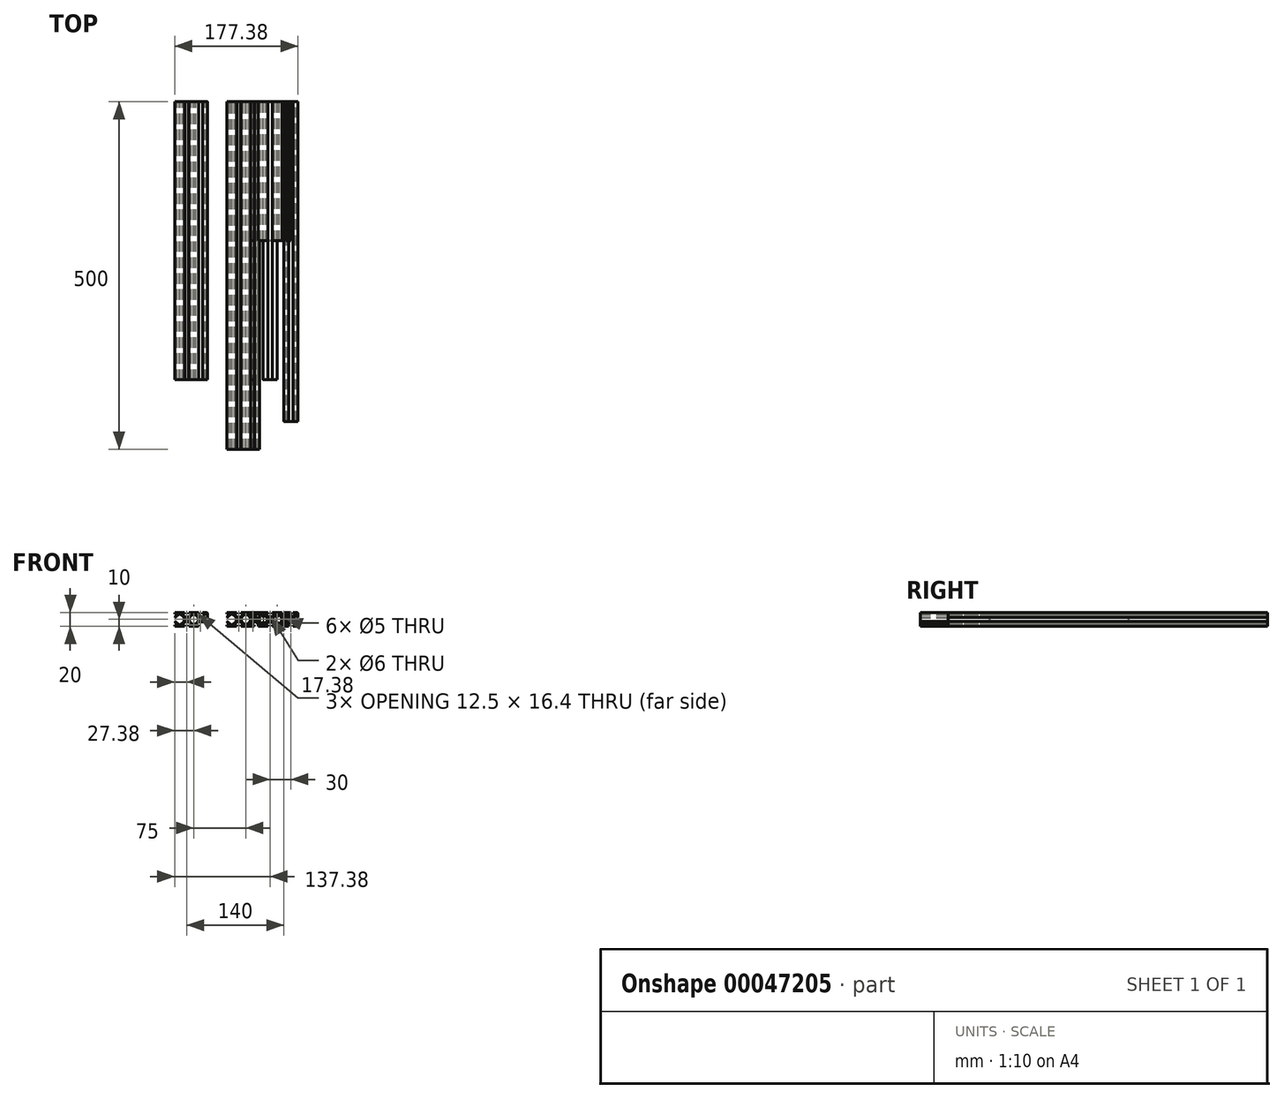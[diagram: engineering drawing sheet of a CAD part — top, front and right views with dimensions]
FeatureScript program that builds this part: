
annotation { "Feature Type Name" : "Feature", "Feature Type Description" : "" }
export const myFeature = defineFeature(function(context is Context, id is Id, definition is map)
    precondition{}
    {
        {
            var Q0;
            Q0=qCreatedBy(makeId("Front.planeOp"),FACE);
            var sketch = newSketch(context, id + "F0", { "sketchPlane" : qUnion([Q0])});
            skLineSegment(sketch, "E0.rect.bottom", {"start": v(8.5, -10) * mm, "end": v(3, -10) * mm});
            skLineSegment(sketch, "E0.rect.top", {"start": v(8.5, 10) * mm, "end": v(3, 10) * mm});
            skLineSegment(sketch, "E0.rect.left", {"start": v(10, -8.5) * mm, "end": v(10, -3) * mm});
            skLineSegment(sketch, "E0.rect.right", {"start": v(-10, -8.5) * mm, "end": v(-10, -3) * mm});
            skPoint(sketch, "E0.rect.middle", {"position": v(0, 0) * mm});
            skCircle(sketch, "E1", {"center": v(0, 0) * mm, "radius": 3 * mm});
            skPoint(sketch, "E2.visualSharp", {"position": v(-10, -10) * mm});
            skArc(sketch, "E2.filletArc", {"start": v(-10, -8.5) * mm, "mid": v(-9.56, -9.56) * mm, "end": v(-8.5, -10) * mm});
            skPoint(sketch, "E3.visualSharp", {"position": v(10, -10) * mm});
            skArc(sketch, "E3.filletArc", {"start": v(8.5, -10) * mm, "mid": v(9.56, -9.56) * mm, "end": v(10, -8.5) * mm});
            skPoint(sketch, "E4.visualSharp", {"position": v(10, 10) * mm});
            skArc(sketch, "E4.filletArc", {"start": v(10, 8.5) * mm, "mid": v(9.56, 9.56) * mm, "end": v(8.5, 10) * mm});
            skPoint(sketch, "E5.visualSharp", {"position": v(-10, 10) * mm});
            skArc(sketch, "E5.filletArc", {"start": v(-8.5, 10) * mm, "mid": v(-9.56, 9.56) * mm, "end": v(-10, 8.5) * mm});
            skLineSegment(sketch, "E6.rect.bottom", {"start": v(4.25, -4.25) * mm, "end": v(-4.25, -4.25) * mm});
            skLineSegment(sketch, "E6.rect.top", {"start": v(4.25, 4.25) * mm, "end": v(-4.25, 4.25) * mm});
            skLineSegment(sketch, "E6.rect.left", {"start": v(4.25, -4.25) * mm, "end": v(4.25, 4.25) * mm});
            skLineSegment(sketch, "E6.rect.right", {"start": v(-4.25, -4.25) * mm, "end": v(-4.25, 4.25) * mm});
            skLineSegment(sketch, "E7", {"start": v(-3, -10) * mm, "end": v(-3, -8.5) * mm});
            skLineSegment(sketch, "E8", {"start": v(-3, -8.5) * mm, "end": v(-6, -8.5) * mm});
            skLineSegment(sketch, "E9", {"start": v(-6, -8.5) * mm, "end": v(-6, -7) * mm});
            skLineSegment(sketch, "E10", {"start": v(-6, -7) * mm, "end": v(-3.25, -4.25) * mm});
            skLineSegment(sketch, "E11.MirrorCS", {"start": v(3, -10) * mm, "end": v(3, -8.5) * mm});
            skLineSegment(sketch, "E12.MirrorCS", {"start": v(3, -8.5) * mm, "end": v(6, -8.5) * mm});
            skLineSegment(sketch, "E13.MirrorCS", {"start": v(6, -8.5) * mm, "end": v(6, -7) * mm});
            skLineSegment(sketch, "E14.MirrorCS", {"start": v(6, -7) * mm, "end": v(3.25, -4.25) * mm});
            skLineSegment(sketch, "E15.MirrorCS", {"start": v(6, 7) * mm, "end": v(3.25, 4.25) * mm});
            skLineSegment(sketch, "E16.MirrorCS", {"start": v(6, 8.5) * mm, "end": v(6, 7) * mm});
            skLineSegment(sketch, "E17.MirrorCS", {"start": v(3, 8.5) * mm, "end": v(6, 8.5) * mm});
            skLineSegment(sketch, "E18.MirrorCS", {"start": v(3, 10) * mm, "end": v(3, 8.5) * mm});
            skLineSegment(sketch, "E19.MirrorCS", {"start": v(-3, 10) * mm, "end": v(-3, 8.5) * mm});
            skLineSegment(sketch, "E20.MirrorCS", {"start": v(-3, 8.5) * mm, "end": v(-6, 8.5) * mm});
            skLineSegment(sketch, "E21.MirrorCS", {"start": v(-6, 8.5) * mm, "end": v(-6, 7) * mm});
            skLineSegment(sketch, "E22.MirrorCS", {"start": v(-6, 7) * mm, "end": v(-3.25, 4.25) * mm});
            skLineSegment(sketch, "E23", {"start": v(-10, -10) * mm, "end": v(10, 10) * mm, "construction": true});
            skLineSegment(sketch, "E24.MirrorCS", {"start": v(-8.5, 3) * mm, "end": v(-8.5, 6) * mm});
            skLineSegment(sketch, "E25.MirrorCS", {"start": v(-8.5, 6) * mm, "end": v(-7, 6) * mm});
            skLineSegment(sketch, "E26.MirrorCS", {"start": v(-10, -3) * mm, "end": v(-8.5, -3) * mm});
            skLineSegment(sketch, "E27.MirrorCS", {"start": v(-10, 3) * mm, "end": v(-8.5, 3) * mm});
            skLineSegment(sketch, "E28.MirrorCS", {"start": v(-8.5, -6) * mm, "end": v(-7, -6) * mm});
            skLineSegment(sketch, "E29.MirrorCS", {"start": v(-8.5, -3) * mm, "end": v(-8.5, -6) * mm});
            skLineSegment(sketch, "E30.MirrorCS", {"start": v(-7, 6) * mm, "end": v(-4.25, 3.25) * mm});
            skLineSegment(sketch, "E31.MirrorCS", {"start": v(-7, -6) * mm, "end": v(-4.25, -3.25) * mm});
            skLineSegment(sketch, "E32.MirrorCS", {"start": v(8.5, -6) * mm, "end": v(7, -6) * mm});
            skLineSegment(sketch, "E33.MirrorCS", {"start": v(8.5, 6) * mm, "end": v(7, 6) * mm});
            skLineSegment(sketch, "E34.MirrorCS", {"start": v(10, 3) * mm, "end": v(8.5, 3) * mm});
            skLineSegment(sketch, "E35.MirrorCS", {"start": v(7, -6) * mm, "end": v(4.25, -3.25) * mm});
            skLineSegment(sketch, "E36.MirrorCS", {"start": v(8.5, -3) * mm, "end": v(8.5, -6) * mm});
            skLineSegment(sketch, "E37.MirrorCS", {"start": v(8.5, 3) * mm, "end": v(8.5, 6) * mm});
            skLineSegment(sketch, "E38.MirrorCS", {"start": v(7, 6) * mm, "end": v(4.25, 3.25) * mm});
            skLineSegment(sketch, "E39.MirrorCS", {"start": v(10, -3) * mm, "end": v(8.5, -3) * mm});
            skLineSegment(sketch, "E40.trimOffspring", {"start": v(-3, -10) * mm, "end": v(-8.5, -10) * mm});
            skLineSegment(sketch, "E41.trimOffspring", {"start": v(10, 3) * mm, "end": v(10, 8.5) * mm});
            skLineSegment(sketch, "E42.trimOffspring", {"start": v(-3, 10) * mm, "end": v(-8.5, 10) * mm});
            skLineSegment(sketch, "E43.trimOffspring", {"start": v(-10, 3) * mm, "end": v(-10, 8.5) * mm});
            skSolve(sketch);
        }
        {
            var Q0;
            Q0=makeQuery(id+"F0.imprint","IMPRINT",FACE,{"disambiguationData":[TD([[makeQuery(id+"F0.imprint","IMPRINT",EDGE,{"derivedFrom":sQuery(id+"F0.wireOp",EDGE,"E0.rect.right")}),-1.0]])]});
            var Q1;
            Q1=makeQuery(id+"F0.imprint","IMPRINT",FACE,{"disambiguationData":[TD([[makeQuery(id+"F0.imprint","IMPRINT",EDGE,{"derivedFrom":sQuery(id+"F0.wireOp",EDGE,"E1")}),-1.0]])]});
            var Q2;
            Q2=makeQuery(id+"F0.imprint","IMPRINT",FACE,{"disambiguationData":[TD([[makeQuery(id+"F0.imprint","IMPRINT",EDGE,{"derivedFrom":sQuery(id+"F0.wireOp",EDGE,"E0.rect.bottom")}),-1.0]])]});
            var Q3;
            Q3=makeQuery(id+"F0.imprint","IMPRINT",FACE,{"disambiguationData":[TD([[makeQuery(id+"F0.imprint","IMPRINT",EDGE,{"derivedFrom":sQuery(id+"F0.wireOp",EDGE,"E0.rect.top")}),1.0]])]});
            var Q4;
            Q4=makeQuery(id+"F0.imprint","IMPRINT",FACE,{"disambiguationData":[TD([[makeQuery(id+"F0.imprint","IMPRINT",EDGE,{"derivedFrom":sQuery(id+"F0.wireOp",EDGE,"E5.filletArc")}),1.0]])]});
            extrude(context, id + "F1", {"entities" : qUnion([Q0, Q1, Q2, Q3, Q4]), "depth" : 460 * mm});
        }
        {
            var Q0;
            Q0=makeQuery(id+"F0.imprint","IMPRINT",FACE,{"disambiguationData":[TD([[makeQuery(id+"F0.imprint","IMPRINT",EDGE,{"derivedFrom":sQuery(id+"F0.wireOp",EDGE,"E0.rect.right")}),-1.0]])]});
            var Q1;
            Q1=makeQuery(id+"F0.imprint","IMPRINT",FACE,{"disambiguationData":[TD([[makeQuery(id+"F0.imprint","IMPRINT",EDGE,{"derivedFrom":sQuery(id+"F0.wireOp",EDGE,"E1")}),-1.0]])]});
            var Q2;
            Q2=makeQuery(id+"F0.imprint","IMPRINT",FACE,{"disambiguationData":[TD([[makeQuery(id+"F0.imprint","IMPRINT",EDGE,{"derivedFrom":sQuery(id+"F0.wireOp",EDGE,"E0.rect.bottom")}),-1.0]])]});
            var Q3;
            Q3=makeQuery(id+"F0.imprint","IMPRINT",FACE,{"disambiguationData":[TD([[makeQuery(id+"F0.imprint","IMPRINT",EDGE,{"derivedFrom":sQuery(id+"F0.wireOp",EDGE,"E0.rect.top")}),1.0]])]});
            var Q4;
            Q4=makeQuery(id+"F0.imprint","IMPRINT",FACE,{"disambiguationData":[TD([[makeQuery(id+"F0.imprint","IMPRINT",EDGE,{"derivedFrom":sQuery(id+"F0.wireOp",EDGE,"E5.filletArc")}),1.0]])]});
            extrude(context, id + "F2", {"entities" : qUnion([Q0, Q1, Q2, Q3, Q4]), "depth" : 400 * mm});
        }
        {
            var Q0;
            Q0=makeQuery(id+"F1.opExtrude","SWEPT_BODY",BODY,{"disambiguationData":[OSD([sQuery(id+"F0.wireOp",EDGE,"E0.rect.bottom"),sQuery(id+"F0.wireOp",EDGE,"E0.rect.top"),sQuery(id+"F0.wireOp",EDGE,"E0.rect.left"),sQuery(id+"F0.wireOp",EDGE,"E0.rect.right"),sQuery(id+"F0.wireOp",EDGE,"E1"),sQuery(id+"F0.wireOp",EDGE,"E2.filletArc"),sQuery(id+"F0.wireOp",EDGE,"E3.filletArc"),sQuery(id+"F0.wireOp",EDGE,"E4.filletArc"),sQuery(id+"F0.wireOp",EDGE,"E5.filletArc"),sQuery(id+"F0.wireOp",EDGE,"E6.rect.bottom"),sQuery(id+"F0.wireOp",EDGE,"E6.rect.top"),sQuery(id+"F0.wireOp",EDGE,"E6.rect.right"),sQuery(id+"F0.wireOp",EDGE,"E7"),sQuery(id+"F0.wireOp",EDGE,"E8"),sQuery(id+"F0.wireOp",EDGE,"E9"),sQuery(id+"F0.wireOp",EDGE,"E10"),sQuery(id+"F0.wireOp",EDGE,"E11.MirrorCS"),sQuery(id+"F0.wireOp",EDGE,"E12.MirrorCS"),sQuery(id+"F0.wireOp",EDGE,"E13.MirrorCS"),sQuery(id+"F0.wireOp",EDGE,"E14.MirrorCS"),sQuery(id+"F0.wireOp",EDGE,"E15.MirrorCS"),sQuery(id+"F0.wireOp",EDGE,"E16.MirrorCS"),sQuery(id+"F0.wireOp",EDGE,"E17.MirrorCS"),sQuery(id+"F0.wireOp",EDGE,"E18.MirrorCS"),sQuery(id+"F0.wireOp",EDGE,"E19.MirrorCS"),sQuery(id+"F0.wireOp",EDGE,"E20.MirrorCS"),sQuery(id+"F0.wireOp",EDGE,"E21.MirrorCS"),sQuery(id+"F0.wireOp",EDGE,"E22.MirrorCS"),sQuery(id+"F0.wireOp",EDGE,"E24.MirrorCS"),sQuery(id+"F0.wireOp",EDGE,"E25.MirrorCS"),sQuery(id+"F0.wireOp",EDGE,"E26.MirrorCS"),sQuery(id+"F0.wireOp",EDGE,"E27.MirrorCS"),sQuery(id+"F0.wireOp",EDGE,"E28.MirrorCS"),sQuery(id+"F0.wireOp",EDGE,"E29.MirrorCS"),sQuery(id+"F0.wireOp",EDGE,"E30.MirrorCS"),sQuery(id+"F0.wireOp",EDGE,"E31.MirrorCS"),sQuery(id+"F0.wireOp",EDGE,"E32.MirrorCS"),sQuery(id+"F0.wireOp",EDGE,"E33.MirrorCS"),sQuery(id+"F0.wireOp",EDGE,"E34.MirrorCS"),sQuery(id+"F0.wireOp",EDGE,"E35.MirrorCS"),sQuery(id+"F0.wireOp",EDGE,"E36.MirrorCS"),sQuery(id+"F0.wireOp",EDGE,"E37.MirrorCS"),sQuery(id+"F0.wireOp",EDGE,"E6.rect.left"),sQuery(id+"F0.wireOp",EDGE,"E38.MirrorCS"),sQuery(id+"F0.wireOp",EDGE,"E39.MirrorCS"),sQuery(id+"F0.wireOp",EDGE,"E40.trimOffspring"),sQuery(id+"F0.wireOp",EDGE,"E41.trimOffspring"),sQuery(id+"F0.wireOp",EDGE,"E42.trimOffspring"),sQuery(id+"F0.wireOp",EDGE,"E43.trimOffspring")])]});
            transform(context, id + "F3", {"entities" : qUnion([Q0]), "transformType" : TransformType.TRANSLATION_3D, "dx" : 30 * mm, "dy" : 0 * mm, "dz" : 0 * mm, "makeCopy" : false});
        }
        {
            var Q0;
            Q0=qCreatedBy(makeId("Front.planeOp"),FACE);
            var sketch = newSketch(context, id + "F4", { "sketchPlane" : qUnion([Q0])});
            skLineSegment(sketch, "E44.rect.bottom", {"start": v(28.5, 10) * mm, "end": v(3, 10) * mm});
            skLineSegment(sketch, "E44.rect.top", {"start": v(28.5, -10) * mm, "end": v(3, -10) * mm});
            skLineSegment(sketch, "E44.rect.left", {"start": v(30, 8.5) * mm, "end": v(30, -8.5) * mm});
            skLineSegment(sketch, "E44.rect.right", {"start": v(-30, 8.5) * mm, "end": v(-30, -8.5) * mm});
            skPoint(sketch, "E44.rect.middle", {"position": v(0, 0) * mm});
            skPoint(sketch, "E45.visualSharp", {"position": v(-30, 10) * mm});
            skArc(sketch, "E45.filletArc", {"start": v(-28.5, 10) * mm, "mid": v(-29.56, 9.56) * mm, "end": v(-30, 8.5) * mm});
            skPoint(sketch, "E46.visualSharp", {"position": v(30, 10) * mm});
            skArc(sketch, "E46.filletArc", {"start": v(30, 8.5) * mm, "mid": v(29.56, 9.56) * mm, "end": v(28.5, 10) * mm});
            skPoint(sketch, "E47.visualSharp", {"position": v(30, -10) * mm});
            skArc(sketch, "E47.filletArc", {"start": v(28.5, -10) * mm, "mid": v(29.56, -9.56) * mm, "end": v(30, -8.5) * mm});
            skPoint(sketch, "E48.visualSharp", {"position": v(-30, -10) * mm});
            skArc(sketch, "E48.filletArc", {"start": v(-30, -8.5) * mm, "mid": v(-29.56, -9.56) * mm, "end": v(-28.5, -10) * mm});
            skCircle(sketch, "E49", {"center": v(0, 0) * mm, "radius": 2.5 * mm});
            skLineSegment(sketch, "E50", {"start": v(-3, 10) * mm, "end": v(-3, 8.2) * mm});
            skLineSegment(sketch, "E51", {"start": v(-3, 8.2) * mm, "end": v(-5.86, 8.2) * mm});
            skLineSegment(sketch, "E52.rect.bottom", {"start": v(3.75, 3.75) * mm, "end": v(-3.75, 3.75) * mm});
            skLineSegment(sketch, "E52.rect.top", {"start": v(3.75, -3.75) * mm, "end": v(-3.75, -3.75) * mm});
            skLineSegment(sketch, "E52.rect.left", {"start": v(3.75, 3.75) * mm, "end": v(3.75, -3.75) * mm});
            skLineSegment(sketch, "E52.rect.right", {"start": v(-3.75, 3.75) * mm, "end": v(-3.75, -3.75) * mm});
            skLineSegment(sketch, "E53", {"start": v(-6.22, 7.35) * mm, "end": v(-2.62, 3.75) * mm});
            skLineSegment(sketch, "E54.MirrorCS", {"start": v(3, 10) * mm, "end": v(3, 8.2) * mm});
            skLineSegment(sketch, "E55.MirrorCS", {"start": v(3, 8.2) * mm, "end": v(5.86, 8.2) * mm});
            skLineSegment(sketch, "E56.MirrorCS", {"start": v(6.22, 7.35) * mm, "end": v(2.62, 3.75) * mm});
            skLineSegment(sketch, "E57", {"start": v(-3.75, 3.75) * mm, "end": v(3.75, -3.75) * mm, "construction": true});
            skLineSegment(sketch, "E58.MirrorCS", {"start": v(-8.2, 7.07) * mm, "end": v(-3.75, 2.62) * mm});
            skLineSegment(sketch, "E59.MirrorCS", {"start": v(-8.2, -7.07) * mm, "end": v(-3.75, -2.62) * mm});
            skLineSegment(sketch, "E60.MirrorCS", {"start": v(-3, -8.2) * mm, "end": v(-5.86, -8.2) * mm});
            skLineSegment(sketch, "E61.MirrorCS", {"start": v(-3, -10) * mm, "end": v(-3, -8.2) * mm});
            skLineSegment(sketch, "E62.MirrorCS", {"start": v(-6.22, -7.35) * mm, "end": v(-2.62, -3.75) * mm});
            skLineSegment(sketch, "E63.MirrorCS", {"start": v(3, -8.2) * mm, "end": v(5.86, -8.2) * mm});
            skLineSegment(sketch, "E64.MirrorCS", {"start": v(6.22, -7.35) * mm, "end": v(2.62, -3.75) * mm});
            skLineSegment(sketch, "E65.MirrorCS", {"start": v(3, -10) * mm, "end": v(3, -8.2) * mm});
            skLineSegment(sketch, "E66", {"start": v(-8.2, 7.07) * mm, "end": v(-9.33, 8.2) * mm});
            skLineSegment(sketch, "E67.trimOffspring", {"start": v(-3, 10) * mm, "end": v(-17, 10) * mm});
            skLineSegment(sketch, "E68.trimOffspring", {"start": v(-3, -10) * mm, "end": v(-17, -10) * mm});
            skPoint(sketch, "E69.visualSharp", {"position": v(-7.07, 8.2) * mm});
            skArc(sketch, "E69.filletArc", {"start": v(-5.86, 8.2) * mm, "mid": v(-6.32, 7.9) * mm, "end": v(-6.22, 7.35) * mm});
            skPoint(sketch, "E70.visualSharp", {"position": v(7.07, 8.2) * mm});
            skArc(sketch, "E70.filletArc", {"start": v(6.22, 7.35) * mm, "mid": v(6.32, 7.9) * mm, "end": v(5.86, 8.2) * mm});
            skPoint(sketch, "E71.visualSharp", {"position": v(7.07, -8.2) * mm});
            skArc(sketch, "E71.filletArc", {"start": v(5.86, -8.2) * mm, "mid": v(6.32, -7.9) * mm, "end": v(6.22, -7.35) * mm});
            skPoint(sketch, "E72.visualSharp", {"position": v(-7.07, -8.2) * mm});
            skArc(sketch, "E72.filletArc", {"start": v(-6.22, -7.35) * mm, "mid": v(-6.32, -7.9) * mm, "end": v(-5.86, -8.2) * mm});
            skLineSegment(sketch, "E73", {"start": v(-10, 13.64) * mm, "end": v(-10, -16.65) * mm, "construction": true});
            skLineSegment(sketch, "E74", {"start": v(-9.33, 8.2) * mm, "end": v(-10, 8.2) * mm});
            skLineSegment(sketch, "E75.MirrorCS", {"start": v(-8.2, -7.07) * mm, "end": v(-9.33, -8.2) * mm});
            skLineSegment(sketch, "E76.MirrorCS", {"start": v(-9.33, -8.2) * mm, "end": v(-10, -8.2) * mm});
            skLineSegment(sketch, "E77.MirrorCS", {"start": v(-17, -10) * mm, "end": v(-17, -8.2) * mm});
            skLineSegment(sketch, "E78.MirrorCS", {"start": v(-11.8, -7.07) * mm, "end": v(-16.25, -2.62) * mm});
            skPoint(sketch, "E79.MirrorP", {"position": v(-20, 0) * mm});
            skLineSegment(sketch, "E80.MirrorCS", {"start": v(-23, -10) * mm, "end": v(-23, -8.2) * mm});
            skLineSegment(sketch, "E81.MirrorCS", {"start": v(-13.78, -7.35) * mm, "end": v(-17.38, -3.75) * mm});
            skPoint(sketch, "E82.MirrorP", {"position": v(-12.93, -8.2) * mm});
            skLineSegment(sketch, "E83.MirrorCS", {"start": v(-23, 8.2) * mm, "end": v(-25.86, 8.2) * mm});
            skLineSegment(sketch, "E84.MirrorCS", {"start": v(-11.8, 7.07) * mm, "end": v(-10.67, 8.2) * mm});
            skPoint(sketch, "E85.MirrorP", {"position": v(-27.07, -8.2) * mm});
            skPoint(sketch, "E86.MirrorP", {"position": v(-12.93, 8.2) * mm});
            skLineSegment(sketch, "E87.MirrorCS", {"start": v(-26.22, -7.35) * mm, "end": v(-22.62, -3.75) * mm});
            skLineSegment(sketch, "E88.MirrorCS", {"start": v(-11.8, -7.07) * mm, "end": v(-10.67, -8.2) * mm});
            skLineSegment(sketch, "E89.MirrorCS", {"start": v(-11.8, 7.07) * mm, "end": v(-16.25, 2.62) * mm});
            skLineSegment(sketch, "E90.MirrorCS", {"start": v(-17, 10) * mm, "end": v(-17, 8.2) * mm});
            skLineSegment(sketch, "E91.MirrorCS", {"start": v(-17, 8.2) * mm, "end": v(-14.14, 8.2) * mm});
            skCircle(sketch, "E92.MirrorC", {"center": v(-20, 0) * mm, "radius": 2.5 * mm});
            skLineSegment(sketch, "E93.MirrorCS", {"start": v(-23, 10) * mm, "end": v(-23, 8.2) * mm});
            skLineSegment(sketch, "E94.MirrorCS", {"start": v(-16.25, 3.75) * mm, "end": v(-23.75, -3.75) * mm, "construction": true});
            skLineSegment(sketch, "E95.MirrorCS", {"start": v(-17, -8.2) * mm, "end": v(-14.14, -8.2) * mm});
            skArc(sketch, "E96.MirrorCS", {"start": v(-25.86, -8.2) * mm, "mid": v(-26.32, -7.9) * mm, "end": v(-26.22, -7.35) * mm});
            skArc(sketch, "E97.MirrorCS", {"start": v(-26.22, 7.35) * mm, "mid": v(-26.32, 7.9) * mm, "end": v(-25.86, 8.2) * mm});
            skArc(sketch, "E98.MirrorCS", {"start": v(-13.78, -7.35) * mm, "mid": v(-13.68, -7.9) * mm, "end": v(-14.14, -8.2) * mm});
            skPoint(sketch, "E99.MirrorP", {"position": v(-27.07, 8.2) * mm});
            skLineSegment(sketch, "E100.MirrorCS", {"start": v(-26.22, 7.35) * mm, "end": v(-22.62, 3.75) * mm});
            skArc(sketch, "E101.MirrorCS", {"start": v(-14.14, 8.2) * mm, "mid": v(-13.68, 7.9) * mm, "end": v(-13.78, 7.35) * mm});
            skLineSegment(sketch, "E102.MirrorCS", {"start": v(-23.75, -3.75) * mm, "end": v(-16.25, -3.75) * mm});
            skLineSegment(sketch, "E103.MirrorCS", {"start": v(-23.75, 3.75) * mm, "end": v(-16.25, 3.75) * mm});
            skLineSegment(sketch, "E104.MirrorCS", {"start": v(-13.78, 7.35) * mm, "end": v(-17.38, 3.75) * mm});
            skLineSegment(sketch, "E105.MirrorCS", {"start": v(-16.25, 3.75) * mm, "end": v(-16.25, -3.75) * mm});
            skLineSegment(sketch, "E106.MirrorCS", {"start": v(-23.75, 3.75) * mm, "end": v(-23.75, -3.75) * mm});
            skLineSegment(sketch, "E107.MirrorCS", {"start": v(-23, -8.2) * mm, "end": v(-25.86, -8.2) * mm});
            skLineSegment(sketch, "E108.MirrorCS", {"start": v(-10.67, 8.2) * mm, "end": v(-10, 8.2) * mm});
            skLineSegment(sketch, "E109.MirrorCS", {"start": v(-10.67, -8.2) * mm, "end": v(-10, -8.2) * mm});
            skLineSegment(sketch, "E110", {"start": v(-20, 13.52) * mm, "end": v(-20, -14.13) * mm, "construction": true});
            skLineSegment(sketch, "E111.MirrorCS", {"start": v(-30, -3) * mm, "end": v(-28.2, -3) * mm});
            skLineSegment(sketch, "E112.MirrorCS", {"start": v(-28.2, -3) * mm, "end": v(-28.2, -5.86) * mm});
            skArc(sketch, "E113.MirrorCS", {"start": v(-28.2, -5.86) * mm, "mid": v(-27.9, -6.32) * mm, "end": v(-27.35, -6.22) * mm});
            skLineSegment(sketch, "E114.MirrorCS", {"start": v(-27.35, -6.22) * mm, "end": v(-23.75, -2.62) * mm});
            skLineSegment(sketch, "E115", {"start": v(-23.75, 3.75) * mm, "end": v(-16.25, -3.75) * mm, "construction": true});
            skLineSegment(sketch, "E116", {"start": v(3.75, 3.75) * mm, "end": v(-3.75, -3.75) * mm, "construction": true});
            skLineSegment(sketch, "E117.MirrorCS", {"start": v(-27.35, 6.22) * mm, "end": v(-23.75, 2.62) * mm});
            skLineSegment(sketch, "E118.MirrorCS", {"start": v(-28.2, 3) * mm, "end": v(-28.2, 5.86) * mm});
            skArc(sketch, "E119.MirrorCS", {"start": v(-27.35, 6.22) * mm, "mid": v(-27.9, 6.32) * mm, "end": v(-28.2, 5.86) * mm});
            skLineSegment(sketch, "E120.MirrorCS", {"start": v(-30, 3) * mm, "end": v(-28.2, 3) * mm});
            skLineSegment(sketch, "E121.trimOffspring", {"start": v(-23, 10) * mm, "end": v(-28.5, 10) * mm});
            skLineSegment(sketch, "E122.trimOffspring", {"start": v(-23, -10) * mm, "end": v(-28.5, -10) * mm});
            skArc(sketch, "E123.MirrorCS", {"start": v(13.78, -7.35) * mm, "mid": v(13.68, -7.9) * mm, "end": v(14.14, -8.2) * mm});
            skLineSegment(sketch, "E124.MirrorCS", {"start": v(10.67, 8.2) * mm, "end": v(10, 8.2) * mm});
            skArc(sketch, "E125.MirrorCS", {"start": v(14.14, 8.2) * mm, "mid": v(13.68, 7.9) * mm, "end": v(13.78, 7.35) * mm});
            skLineSegment(sketch, "E126.MirrorCS", {"start": v(11.8, 7.07) * mm, "end": v(10.67, 8.2) * mm});
            skLineSegment(sketch, "E127.MirrorCS", {"start": v(8.2, 7.07) * mm, "end": v(9.33, 8.2) * mm});
            skArc(sketch, "E128.MirrorCS", {"start": v(6.22, -7.35) * mm, "mid": v(6.32, -7.9) * mm, "end": v(5.86, -8.2) * mm});
            skArc(sketch, "E129.MirrorCS", {"start": v(26.22, 7.35) * mm, "mid": v(26.32, 7.9) * mm, "end": v(25.86, 8.2) * mm});
            skArc(sketch, "E130.MirrorCS", {"start": v(28.2, -5.86) * mm, "mid": v(27.9, -6.32) * mm, "end": v(27.35, -6.22) * mm});
            skArc(sketch, "E131.MirrorCS", {"start": v(25.86, -8.2) * mm, "mid": v(26.32, -7.9) * mm, "end": v(26.22, -7.35) * mm});
            skLineSegment(sketch, "E132.MirrorCS", {"start": v(10.67, -8.2) * mm, "end": v(10, -8.2) * mm});
            skLineSegment(sketch, "E133.MirrorCS", {"start": v(8.2, -7.07) * mm, "end": v(9.33, -8.2) * mm});
            skArc(sketch, "E134.MirrorCS", {"start": v(5.86, 8.2) * mm, "mid": v(6.32, 7.9) * mm, "end": v(6.22, 7.35) * mm});
            skLineSegment(sketch, "E135.MirrorCS", {"start": v(9.33, 8.2) * mm, "end": v(10, 8.2) * mm});
            skArc(sketch, "E136.MirrorCS", {"start": v(27.35, 6.22) * mm, "mid": v(27.9, 6.32) * mm, "end": v(28.2, 5.86) * mm});
            skLineSegment(sketch, "E137.MirrorCS", {"start": v(9.33, -8.2) * mm, "end": v(10, -8.2) * mm});
            skLineSegment(sketch, "E138.MirrorCS", {"start": v(11.8, -7.07) * mm, "end": v(10.67, -8.2) * mm});
            skLineSegment(sketch, "E139.MirrorCS", {"start": v(8.2, -7.07) * mm, "end": v(3.75, -2.62) * mm});
            skPoint(sketch, "E140.MirrorP", {"position": v(20, 0) * mm});
            skArc(sketch, "E141.MirrorCS", {"start": v(30, -8.5) * mm, "mid": v(29.56, -9.56) * mm, "end": v(28.5, -10) * mm});
            skArc(sketch, "E142.MirrorCS", {"start": v(28.5, 10) * mm, "mid": v(29.56, 9.56) * mm, "end": v(30, 8.5) * mm});
            skLineSegment(sketch, "E143.MirrorCS", {"start": v(23, 10) * mm, "end": v(23, 8.2) * mm});
            skLineSegment(sketch, "E144.MirrorCS", {"start": v(17, -10) * mm, "end": v(17, -8.2) * mm});
            skLineSegment(sketch, "E145.MirrorCS", {"start": v(11.8, -7.07) * mm, "end": v(16.25, -2.62) * mm});
            skLineSegment(sketch, "E146.MirrorCS", {"start": v(27.35, -6.22) * mm, "end": v(23.75, -2.62) * mm});
            skCircle(sketch, "E147.MirrorC", {"center": v(20, 0) * mm, "radius": 2.5 * mm});
            skLineSegment(sketch, "E148.MirrorCS", {"start": v(23, -10) * mm, "end": v(28.5, -10) * mm});
            skLineSegment(sketch, "E149.MirrorCS", {"start": v(23.75, 3.75) * mm, "end": v(16.25, -3.75) * mm, "construction": true});
            skPoint(sketch, "E150.MirrorP", {"position": v(27.07, -8.2) * mm});
            skLineSegment(sketch, "E151.MirrorCS", {"start": v(8.2, 7.07) * mm, "end": v(3.75, 2.62) * mm});
            skLineSegment(sketch, "E152.MirrorCS", {"start": v(17, 8.2) * mm, "end": v(14.14, 8.2) * mm});
            skLineSegment(sketch, "E153.MirrorCS", {"start": v(23, 8.2) * mm, "end": v(25.86, 8.2) * mm});
            skLineSegment(sketch, "E154.MirrorCS", {"start": v(23, -8.2) * mm, "end": v(25.86, -8.2) * mm});
            skLineSegment(sketch, "E155.MirrorCS", {"start": v(26.22, 7.35) * mm, "end": v(22.62, 3.75) * mm});
            skLineSegment(sketch, "E156.MirrorCS", {"start": v(23, -10) * mm, "end": v(23, -8.2) * mm});
            skPoint(sketch, "E157.MirrorP", {"position": v(12.93, 8.2) * mm});
            skPoint(sketch, "E158.MirrorP", {"position": v(12.93, -8.2) * mm});
            skLineSegment(sketch, "E159.MirrorCS", {"start": v(23, 10) * mm, "end": v(28.5, 10) * mm});
            skLineSegment(sketch, "E160.MirrorCS", {"start": v(17, 10) * mm, "end": v(17, 8.2) * mm});
            skLineSegment(sketch, "E161.MirrorCS", {"start": v(23.75, 3.75) * mm, "end": v(23.75, -3.75) * mm});
            skPoint(sketch, "E162.MirrorP", {"position": v(27.07, 8.2) * mm});
            skLineSegment(sketch, "E163.MirrorCS", {"start": v(17, -8.2) * mm, "end": v(14.14, -8.2) * mm});
            skLineSegment(sketch, "E164.MirrorCS", {"start": v(30, -3) * mm, "end": v(28.2, -3) * mm});
            skLineSegment(sketch, "E165.MirrorCS", {"start": v(28.2, -3) * mm, "end": v(28.2, -5.86) * mm});
            skLineSegment(sketch, "E166.MirrorCS", {"start": v(16.25, 3.75) * mm, "end": v(16.25, -3.75) * mm});
            skLineSegment(sketch, "E167.MirrorCS", {"start": v(13.78, -7.35) * mm, "end": v(17.38, -3.75) * mm});
            skLineSegment(sketch, "E168.MirrorCS", {"start": v(27.35, 6.22) * mm, "end": v(23.75, 2.62) * mm});
            skLineSegment(sketch, "E169.MirrorCS", {"start": v(23.75, -3.75) * mm, "end": v(16.25, -3.75) * mm});
            skLineSegment(sketch, "E170.MirrorCS", {"start": v(28.2, 3) * mm, "end": v(28.2, 5.86) * mm});
            skLineSegment(sketch, "E171.MirrorCS", {"start": v(30, 3) * mm, "end": v(28.2, 3) * mm});
            skLineSegment(sketch, "E172.MirrorCS", {"start": v(16.25, 3.75) * mm, "end": v(23.75, -3.75) * mm, "construction": true});
            skLineSegment(sketch, "E173.MirrorCS", {"start": v(13.78, 7.35) * mm, "end": v(17.38, 3.75) * mm});
            skLineSegment(sketch, "E174.MirrorCS", {"start": v(11.8, 7.07) * mm, "end": v(16.25, 2.62) * mm});
            skLineSegment(sketch, "E175.MirrorCS", {"start": v(26.22, -7.35) * mm, "end": v(22.62, -3.75) * mm});
            skLineSegment(sketch, "E176.MirrorCS", {"start": v(3, -10) * mm, "end": v(20, -10) * mm});
            skLineSegment(sketch, "E177.MirrorCS", {"start": v(23.75, 3.75) * mm, "end": v(16.25, 3.75) * mm});
            skLineSegment(sketch, "E178.MirrorCS", {"start": v(3, 10) * mm, "end": v(17, 10) * mm});
            skPoint(sketch, "E179.orphan", {"position": v(-20, -10) * mm});
            skSolve(sketch);
        }
        {
            var Q0;
            {var subQ5=sQuery(id+"F4.wireOp",EDGE,"E45.filletArc");Q0=makeQuery(id+"F4.imprint","IMPRINT",FACE,{"disambiguationData":[TD([[makeQuery(id+"F4.imprint","IMPRINT",EDGE,{"derivedFrom":subQ5}),1.0]])]});}
            var Q1;
            Q1=makeQuery(id+"F4.imprint","IMPRINT",FACE,{"disambiguationData":[TD([[makeQuery(id+"F4.imprint","IMPRINT",EDGE,{"derivedFrom":sQuery(id+"F4.wireOp",EDGE,"E92.MirrorC")}),1.0]])]});
            var Q2;
            Q2=makeQuery(id+"F4.imprint","IMPRINT",FACE,{"disambiguationData":[TD([[makeQuery(id+"F4.imprint","IMPRINT",EDGE,{"derivedFrom":sQuery(id+"F4.wireOp",EDGE,"E50")}),-1.0]])]});
            var Q3;
            Q3=makeQuery(id+"F4.imprint","IMPRINT",FACE,{"disambiguationData":[TD([[makeQuery(id+"F4.imprint","IMPRINT",EDGE,{"derivedFrom":sQuery(id+"F4.wireOp",EDGE,"E49")}),-1.0]])]});
            var Q4;
            Q4=makeQuery(id+"F4.imprint","IMPRINT",FACE,{"disambiguationData":[TD([[makeQuery(id+"F4.imprint","IMPRINT",EDGE,{"derivedFrom":sQuery(id+"F4.wireOp",EDGE,"E124.MirrorCS")}),-1.0]])]});
            var Q5;
            Q5=makeQuery(id+"F4.imprint","IMPRINT",FACE,{"disambiguationData":[TD([[makeQuery(id+"F4.imprint","IMPRINT",EDGE,{"derivedFrom":sQuery(id+"F4.wireOp",EDGE,"E147.MirrorC")}),-1.0]])]});
            var Q6;
            Q6=makeQuery(id+"F4.imprint","IMPRINT",FACE,{"disambiguationData":[TD([[makeQuery(id+"F4.imprint","IMPRINT",EDGE,{"derivedFrom":sQuery(id+"F4.wireOp",EDGE,"E129.MirrorCS")}),-1.0]])]});
            var Q7;
            Q7=makeQuery(id+"F4.imprint","IMPRINT",FACE,{"disambiguationData":[TD([[makeQuery(id+"F4.imprint","IMPRINT",EDGE,{"derivedFrom":sQuery(id+"F4.wireOp",EDGE,"E130.MirrorCS")}),1.0]])]});
            var Q8;
            Q8=makeQuery(id+"F4.imprint","IMPRINT",FACE,{"disambiguationData":[TD([[makeQuery(id+"F4.imprint","IMPRINT",EDGE,{"derivedFrom":sQuery(id+"F4.wireOp",EDGE,"E123.MirrorCS")}),-1.0]])]});
            var Q9;
            Q9=makeQuery(id+"F4.imprint","IMPRINT",FACE,{"disambiguationData":[TD([[makeQuery(id+"F4.imprint","IMPRINT",EDGE,{"derivedFrom":sQuery(id+"F4.wireOp",EDGE,"E60.MirrorCS")}),1.0]])]});
            var Q10;
            {var subQ5=sQuery(id+"F4.wireOp",EDGE,"E48.filletArc");Q10=makeQuery(id+"F4.imprint","IMPRINT",FACE,{"disambiguationData":[TD([[makeQuery(id+"F4.imprint","IMPRINT",EDGE,{"derivedFrom":subQ5}),1.0]])]});}
            extrude(context, id + "F5", {"entities" : qUnion([Q0, Q1, Q2, Q3, Q4, Q5, Q6, Q7, Q8, Q9, Q10]), "depth" : 500 * mm});
        }
        {
            var Q0;
            {var subQ5=sQuery(id+"F4.wireOp",EDGE,"E45.filletArc");Q0=makeQuery(id+"F4.imprint","IMPRINT",FACE,{"disambiguationData":[TD([[makeQuery(id+"F4.imprint","IMPRINT",EDGE,{"derivedFrom":subQ5}),1.0]])]});}
            var Q1;
            Q1=makeQuery(id+"F4.imprint","IMPRINT",FACE,{"disambiguationData":[TD([[makeQuery(id+"F4.imprint","IMPRINT",EDGE,{"derivedFrom":sQuery(id+"F4.wireOp",EDGE,"E92.MirrorC")}),1.0]])]});
            var Q2;
            Q2=makeQuery(id+"F4.imprint","IMPRINT",FACE,{"disambiguationData":[TD([[makeQuery(id+"F4.imprint","IMPRINT",EDGE,{"derivedFrom":sQuery(id+"F4.wireOp",EDGE,"E50")}),-1.0]])]});
            var Q3;
            Q3=makeQuery(id+"F4.imprint","IMPRINT",FACE,{"disambiguationData":[TD([[makeQuery(id+"F4.imprint","IMPRINT",EDGE,{"derivedFrom":sQuery(id+"F4.wireOp",EDGE,"E49")}),-1.0]])]});
            var Q4;
            Q4=makeQuery(id+"F4.imprint","IMPRINT",FACE,{"disambiguationData":[TD([[makeQuery(id+"F4.imprint","IMPRINT",EDGE,{"derivedFrom":sQuery(id+"F4.wireOp",EDGE,"E124.MirrorCS")}),-1.0]])]});
            var Q5;
            Q5=makeQuery(id+"F4.imprint","IMPRINT",FACE,{"disambiguationData":[TD([[makeQuery(id+"F4.imprint","IMPRINT",EDGE,{"derivedFrom":sQuery(id+"F4.wireOp",EDGE,"E147.MirrorC")}),-1.0]])]});
            var Q6;
            Q6=makeQuery(id+"F4.imprint","IMPRINT",FACE,{"disambiguationData":[TD([[makeQuery(id+"F4.imprint","IMPRINT",EDGE,{"derivedFrom":sQuery(id+"F4.wireOp",EDGE,"E129.MirrorCS")}),-1.0]])]});
            var Q7;
            Q7=makeQuery(id+"F4.imprint","IMPRINT",FACE,{"disambiguationData":[TD([[makeQuery(id+"F4.imprint","IMPRINT",EDGE,{"derivedFrom":sQuery(id+"F4.wireOp",EDGE,"E130.MirrorCS")}),1.0]])]});
            var Q8;
            Q8=makeQuery(id+"F4.imprint","IMPRINT",FACE,{"disambiguationData":[TD([[makeQuery(id+"F4.imprint","IMPRINT",EDGE,{"derivedFrom":sQuery(id+"F4.wireOp",EDGE,"E123.MirrorCS")}),-1.0]])]});
            var Q9;
            Q9=makeQuery(id+"F4.imprint","IMPRINT",FACE,{"disambiguationData":[TD([[makeQuery(id+"F4.imprint","IMPRINT",EDGE,{"derivedFrom":sQuery(id+"F4.wireOp",EDGE,"E60.MirrorCS")}),1.0]])]});
            var Q10;
            {var subQ5=sQuery(id+"F4.wireOp",EDGE,"E48.filletArc");Q10=makeQuery(id+"F4.imprint","IMPRINT",FACE,{"disambiguationData":[TD([[makeQuery(id+"F4.imprint","IMPRINT",EDGE,{"derivedFrom":subQ5}),1.0]])]});}
            extrude(context, id + "F6", {"entities" : qUnion([Q0, Q1, Q2, Q3, Q4, Q5, Q6, Q7, Q8, Q9, Q10]), "depth" : 400 * mm});
        }
        {
            var Q0;
            Q0=makeQuery(id+"F5.opExtrude","SWEPT_BODY",BODY,{"disambiguationData":[OSD([sQuery(id+"F4.wireOp",EDGE,"E44.rect.right"),sQuery(id+"F4.wireOp",EDGE,"E45.filletArc"),sQuery(id+"F4.wireOp",EDGE,"E48.filletArc"),sQuery(id+"F4.wireOp",EDGE,"E49"),sQuery(id+"F4.wireOp",EDGE,"E50"),sQuery(id+"F4.wireOp",EDGE,"E51"),sQuery(id+"F4.wireOp",EDGE,"E52.rect.bottom"),sQuery(id+"F4.wireOp",EDGE,"E52.rect.top"),sQuery(id+"F4.wireOp",EDGE,"E52.rect.right"),sQuery(id+"F4.wireOp",EDGE,"E53"),sQuery(id+"F4.wireOp",EDGE,"E58.MirrorCS"),sQuery(id+"F4.wireOp",EDGE,"E60.MirrorCS"),sQuery(id+"F4.wireOp",EDGE,"E62.MirrorCS"),sQuery(id+"F4.wireOp",EDGE,"E59.MirrorCS"),sQuery(id+"F4.wireOp",EDGE,"E61.MirrorCS"),sQuery(id+"F4.wireOp",EDGE,"E66"),sQuery(id+"F4.wireOp",EDGE,"E67.trimOffspring"),sQuery(id+"F4.wireOp",EDGE,"E68.trimOffspring"),sQuery(id+"F4.wireOp",EDGE,"E69.filletArc"),sQuery(id+"F4.wireOp",EDGE,"E72.filletArc"),sQuery(id+"F4.wireOp",EDGE,"E74"),sQuery(id+"F4.wireOp",EDGE,"E75.MirrorCS"),sQuery(id+"F4.wireOp",EDGE,"E76.MirrorCS"),sQuery(id+"F4.wireOp",EDGE,"E80.MirrorCS"),sQuery(id+"F4.wireOp",EDGE,"E81.MirrorCS"),sQuery(id+"F4.wireOp",EDGE,"E83.MirrorCS"),sQuery(id+"F4.wireOp",EDGE,"E84.MirrorCS"),sQuery(id+"F4.wireOp",EDGE,"E87.MirrorCS"),sQuery(id+"F4.wireOp",EDGE,"E88.MirrorCS"),sQuery(id+"F4.wireOp",EDGE,"E89.MirrorCS"),sQuery(id+"F4.wireOp",EDGE,"E77.MirrorCS"),sQuery(id+"F4.wireOp",EDGE,"E90.MirrorCS"),sQuery(id+"F4.wireOp",EDGE,"E91.MirrorCS"),sQuery(id+"F4.wireOp",EDGE,"E92.MirrorC"),sQuery(id+"F4.wireOp",EDGE,"E78.MirrorCS"),sQuery(id+"F4.wireOp",EDGE,"E95.MirrorCS"),sQuery(id+"F4.wireOp",EDGE,"E96.MirrorCS"),sQuery(id+"F4.wireOp",EDGE,"E97.MirrorCS"),sQuery(id+"F4.wireOp",EDGE,"E98.MirrorCS"),sQuery(id+"F4.wireOp",EDGE,"E100.MirrorCS"),sQuery(id+"F4.wireOp",EDGE,"E101.MirrorCS"),sQuery(id+"F4.wireOp",EDGE,"E102.MirrorCS"),sQuery(id+"F4.wireOp",EDGE,"E103.MirrorCS"),sQuery(id+"F4.wireOp",EDGE,"E104.MirrorCS"),sQuery(id+"F4.wireOp",EDGE,"E105.MirrorCS"),sQuery(id+"F4.wireOp",EDGE,"E106.MirrorCS"),sQuery(id+"F4.wireOp",EDGE,"E107.MirrorCS"),sQuery(id+"F4.wireOp",EDGE,"E108.MirrorCS"),sQuery(id+"F4.wireOp",EDGE,"E109.MirrorCS"),sQuery(id+"F4.wireOp",EDGE,"E93.MirrorCS"),sQuery(id+"F4.wireOp",EDGE,"E111.MirrorCS"),sQuery(id+"F4.wireOp",EDGE,"E112.MirrorCS"),sQuery(id+"F4.wireOp",EDGE,"E113.MirrorCS"),sQuery(id+"F4.wireOp",EDGE,"E114.MirrorCS"),sQuery(id+"F4.wireOp",EDGE,"E117.MirrorCS"),sQuery(id+"F4.wireOp",EDGE,"E118.MirrorCS"),sQuery(id+"F4.wireOp",EDGE,"E119.MirrorCS"),sQuery(id+"F4.wireOp",EDGE,"E120.MirrorCS"),sQuery(id+"F4.wireOp",EDGE,"E121.trimOffspring"),sQuery(id+"F4.wireOp",EDGE,"E122.trimOffspring"),sQuery(id+"F4.wireOp",EDGE,"E123.MirrorCS"),sQuery(id+"F4.wireOp",EDGE,"E124.MirrorCS"),sQuery(id+"F4.wireOp",EDGE,"E125.MirrorCS"),sQuery(id+"F4.wireOp",EDGE,"E126.MirrorCS"),sQuery(id+"F4.wireOp",EDGE,"E127.MirrorCS"),sQuery(id+"F4.wireOp",EDGE,"E128.MirrorCS"),sQuery(id+"F4.wireOp",EDGE,"E129.MirrorCS"),sQuery(id+"F4.wireOp",EDGE,"E130.MirrorCS"),sQuery(id+"F4.wireOp",EDGE,"E131.MirrorCS"),sQuery(id+"F4.wireOp",EDGE,"E132.MirrorCS"),sQuery(id+"F4.wireOp",EDGE,"E133.MirrorCS"),sQuery(id+"F4.wireOp",EDGE,"E134.MirrorCS"),sQuery(id+"F4.wireOp",EDGE,"E135.MirrorCS"),sQuery(id+"F4.wireOp",EDGE,"E136.MirrorCS"),sQuery(id+"F4.wireOp",EDGE,"E137.MirrorCS"),sQuery(id+"F4.wireOp",EDGE,"E138.MirrorCS"),sQuery(id+"F4.wireOp",EDGE,"E141.MirrorCS"),sQuery(id+"F4.wireOp",EDGE,"E142.MirrorCS"),sQuery(id+"F4.wireOp",EDGE,"E146.MirrorCS"),sQuery(id+"F4.wireOp",EDGE,"E147.MirrorC"),sQuery(id+"F4.wireOp",EDGE,"E148.MirrorCS"),sQuery(id+"F4.wireOp",EDGE,"E151.MirrorCS"),sQuery(id+"F4.wireOp",EDGE,"E65.MirrorCS"),sQuery(id+"F4.wireOp",EDGE,"E152.MirrorCS"),sQuery(id+"F4.wireOp",EDGE,"E153.MirrorCS"),sQuery(id+"F4.wireOp",EDGE,"E154.MirrorCS"),sQuery(id+"F4.wireOp",EDGE,"E155.MirrorCS"),sQuery(id+"F4.wireOp",EDGE,"E156.MirrorCS"),sQuery(id+"F4.wireOp",EDGE,"E55.MirrorCS"),sQuery(id+"F4.wireOp",EDGE,"E54.MirrorCS"),sQuery(id+"F4.wireOp",EDGE,"E159.MirrorCS"),sQuery(id+"F4.wireOp",EDGE,"E160.MirrorCS"),sQuery(id+"F4.wireOp",EDGE,"E161.MirrorCS"),sQuery(id+"F4.wireOp",EDGE,"E44.rect.left"),sQuery(id+"F4.wireOp",EDGE,"E163.MirrorCS"),sQuery(id+"F4.wireOp",EDGE,"E164.MirrorCS"),sQuery(id+"F4.wireOp",EDGE,"E139.MirrorCS"),sQuery(id+"F4.wireOp",EDGE,"E56.MirrorCS"),sQuery(id+"F4.wireOp",EDGE,"E165.MirrorCS"),sQuery(id+"F4.wireOp",EDGE,"E144.MirrorCS"),sQuery(id+"F4.wireOp",EDGE,"E166.MirrorCS"),sQuery(id+"F4.wireOp",EDGE,"E167.MirrorCS"),sQuery(id+"F4.wireOp",EDGE,"E145.MirrorCS"),sQuery(id+"F4.wireOp",EDGE,"E168.MirrorCS"),sQuery(id+"F4.wireOp",EDGE,"E169.MirrorCS"),sQuery(id+"F4.wireOp",EDGE,"E170.MirrorCS"),sQuery(id+"F4.wireOp",EDGE,"E52.rect.left"),sQuery(id+"F4.wireOp",EDGE,"E171.MirrorCS"),sQuery(id+"F4.wireOp",EDGE,"E173.MirrorCS"),sQuery(id+"F4.wireOp",EDGE,"E174.MirrorCS"),sQuery(id+"F4.wireOp",EDGE,"E175.MirrorCS"),sQuery(id+"F4.wireOp",EDGE,"E176.MirrorCS"),sQuery(id+"F4.wireOp",EDGE,"E63.MirrorCS"),sQuery(id+"F4.wireOp",EDGE,"E143.MirrorCS"),sQuery(id+"F4.wireOp",EDGE,"E64.MirrorCS"),sQuery(id+"F4.wireOp",EDGE,"E177.MirrorCS"),sQuery(id+"F4.wireOp",EDGE,"E178.MirrorCS")])]});
            transform(context, id + "F7", {"entities" : qUnion([Q0]), "transformType" : TransformType.TRANSLATION_3D, "dx" : -45 * mm, "dy" : 0 * mm, "dz" : 0 * mm, "makeCopy" : false});
        }
        {
            var Q0;
            Q0=makeQuery(id+"F6.opExtrude","SWEPT_BODY",BODY,{"disambiguationData":[OSD([sQuery(id+"F4.wireOp",EDGE,"E44.rect.right"),sQuery(id+"F4.wireOp",EDGE,"E45.filletArc"),sQuery(id+"F4.wireOp",EDGE,"E48.filletArc"),sQuery(id+"F4.wireOp",EDGE,"E49"),sQuery(id+"F4.wireOp",EDGE,"E50"),sQuery(id+"F4.wireOp",EDGE,"E51"),sQuery(id+"F4.wireOp",EDGE,"E52.rect.bottom"),sQuery(id+"F4.wireOp",EDGE,"E52.rect.top"),sQuery(id+"F4.wireOp",EDGE,"E52.rect.right"),sQuery(id+"F4.wireOp",EDGE,"E53"),sQuery(id+"F4.wireOp",EDGE,"E58.MirrorCS"),sQuery(id+"F4.wireOp",EDGE,"E60.MirrorCS"),sQuery(id+"F4.wireOp",EDGE,"E62.MirrorCS"),sQuery(id+"F4.wireOp",EDGE,"E59.MirrorCS"),sQuery(id+"F4.wireOp",EDGE,"E61.MirrorCS"),sQuery(id+"F4.wireOp",EDGE,"E66"),sQuery(id+"F4.wireOp",EDGE,"E67.trimOffspring"),sQuery(id+"F4.wireOp",EDGE,"E68.trimOffspring"),sQuery(id+"F4.wireOp",EDGE,"E69.filletArc"),sQuery(id+"F4.wireOp",EDGE,"E72.filletArc"),sQuery(id+"F4.wireOp",EDGE,"E74"),sQuery(id+"F4.wireOp",EDGE,"E75.MirrorCS"),sQuery(id+"F4.wireOp",EDGE,"E76.MirrorCS"),sQuery(id+"F4.wireOp",EDGE,"E80.MirrorCS"),sQuery(id+"F4.wireOp",EDGE,"E81.MirrorCS"),sQuery(id+"F4.wireOp",EDGE,"E83.MirrorCS"),sQuery(id+"F4.wireOp",EDGE,"E84.MirrorCS"),sQuery(id+"F4.wireOp",EDGE,"E87.MirrorCS"),sQuery(id+"F4.wireOp",EDGE,"E88.MirrorCS"),sQuery(id+"F4.wireOp",EDGE,"E89.MirrorCS"),sQuery(id+"F4.wireOp",EDGE,"E77.MirrorCS"),sQuery(id+"F4.wireOp",EDGE,"E90.MirrorCS"),sQuery(id+"F4.wireOp",EDGE,"E91.MirrorCS"),sQuery(id+"F4.wireOp",EDGE,"E92.MirrorC"),sQuery(id+"F4.wireOp",EDGE,"E78.MirrorCS"),sQuery(id+"F4.wireOp",EDGE,"E95.MirrorCS"),sQuery(id+"F4.wireOp",EDGE,"E96.MirrorCS"),sQuery(id+"F4.wireOp",EDGE,"E97.MirrorCS"),sQuery(id+"F4.wireOp",EDGE,"E98.MirrorCS"),sQuery(id+"F4.wireOp",EDGE,"E100.MirrorCS"),sQuery(id+"F4.wireOp",EDGE,"E101.MirrorCS"),sQuery(id+"F4.wireOp",EDGE,"E102.MirrorCS"),sQuery(id+"F4.wireOp",EDGE,"E103.MirrorCS"),sQuery(id+"F4.wireOp",EDGE,"E104.MirrorCS"),sQuery(id+"F4.wireOp",EDGE,"E105.MirrorCS"),sQuery(id+"F4.wireOp",EDGE,"E106.MirrorCS"),sQuery(id+"F4.wireOp",EDGE,"E107.MirrorCS"),sQuery(id+"F4.wireOp",EDGE,"E108.MirrorCS"),sQuery(id+"F4.wireOp",EDGE,"E109.MirrorCS"),sQuery(id+"F4.wireOp",EDGE,"E93.MirrorCS"),sQuery(id+"F4.wireOp",EDGE,"E111.MirrorCS"),sQuery(id+"F4.wireOp",EDGE,"E112.MirrorCS"),sQuery(id+"F4.wireOp",EDGE,"E113.MirrorCS"),sQuery(id+"F4.wireOp",EDGE,"E114.MirrorCS"),sQuery(id+"F4.wireOp",EDGE,"E117.MirrorCS"),sQuery(id+"F4.wireOp",EDGE,"E118.MirrorCS"),sQuery(id+"F4.wireOp",EDGE,"E119.MirrorCS"),sQuery(id+"F4.wireOp",EDGE,"E120.MirrorCS"),sQuery(id+"F4.wireOp",EDGE,"E121.trimOffspring"),sQuery(id+"F4.wireOp",EDGE,"E122.trimOffspring"),sQuery(id+"F4.wireOp",EDGE,"E123.MirrorCS"),sQuery(id+"F4.wireOp",EDGE,"E124.MirrorCS"),sQuery(id+"F4.wireOp",EDGE,"E125.MirrorCS"),sQuery(id+"F4.wireOp",EDGE,"E126.MirrorCS"),sQuery(id+"F4.wireOp",EDGE,"E127.MirrorCS"),sQuery(id+"F4.wireOp",EDGE,"E128.MirrorCS"),sQuery(id+"F4.wireOp",EDGE,"E129.MirrorCS"),sQuery(id+"F4.wireOp",EDGE,"E130.MirrorCS"),sQuery(id+"F4.wireOp",EDGE,"E131.MirrorCS"),sQuery(id+"F4.wireOp",EDGE,"E132.MirrorCS"),sQuery(id+"F4.wireOp",EDGE,"E133.MirrorCS"),sQuery(id+"F4.wireOp",EDGE,"E134.MirrorCS"),sQuery(id+"F4.wireOp",EDGE,"E135.MirrorCS"),sQuery(id+"F4.wireOp",EDGE,"E136.MirrorCS"),sQuery(id+"F4.wireOp",EDGE,"E137.MirrorCS"),sQuery(id+"F4.wireOp",EDGE,"E138.MirrorCS"),sQuery(id+"F4.wireOp",EDGE,"E141.MirrorCS"),sQuery(id+"F4.wireOp",EDGE,"E142.MirrorCS"),sQuery(id+"F4.wireOp",EDGE,"E146.MirrorCS"),sQuery(id+"F4.wireOp",EDGE,"E147.MirrorC"),sQuery(id+"F4.wireOp",EDGE,"E148.MirrorCS"),sQuery(id+"F4.wireOp",EDGE,"E151.MirrorCS"),sQuery(id+"F4.wireOp",EDGE,"E65.MirrorCS"),sQuery(id+"F4.wireOp",EDGE,"E152.MirrorCS"),sQuery(id+"F4.wireOp",EDGE,"E153.MirrorCS"),sQuery(id+"F4.wireOp",EDGE,"E154.MirrorCS"),sQuery(id+"F4.wireOp",EDGE,"E155.MirrorCS"),sQuery(id+"F4.wireOp",EDGE,"E156.MirrorCS"),sQuery(id+"F4.wireOp",EDGE,"E55.MirrorCS"),sQuery(id+"F4.wireOp",EDGE,"E54.MirrorCS"),sQuery(id+"F4.wireOp",EDGE,"E159.MirrorCS"),sQuery(id+"F4.wireOp",EDGE,"E160.MirrorCS"),sQuery(id+"F4.wireOp",EDGE,"E161.MirrorCS"),sQuery(id+"F4.wireOp",EDGE,"E44.rect.left"),sQuery(id+"F4.wireOp",EDGE,"E163.MirrorCS"),sQuery(id+"F4.wireOp",EDGE,"E164.MirrorCS"),sQuery(id+"F4.wireOp",EDGE,"E139.MirrorCS"),sQuery(id+"F4.wireOp",EDGE,"E56.MirrorCS"),sQuery(id+"F4.wireOp",EDGE,"E165.MirrorCS"),sQuery(id+"F4.wireOp",EDGE,"E144.MirrorCS"),sQuery(id+"F4.wireOp",EDGE,"E166.MirrorCS"),sQuery(id+"F4.wireOp",EDGE,"E167.MirrorCS"),sQuery(id+"F4.wireOp",EDGE,"E145.MirrorCS"),sQuery(id+"F4.wireOp",EDGE,"E168.MirrorCS"),sQuery(id+"F4.wireOp",EDGE,"E169.MirrorCS"),sQuery(id+"F4.wireOp",EDGE,"E170.MirrorCS"),sQuery(id+"F4.wireOp",EDGE,"E52.rect.left"),sQuery(id+"F4.wireOp",EDGE,"E171.MirrorCS"),sQuery(id+"F4.wireOp",EDGE,"E173.MirrorCS"),sQuery(id+"F4.wireOp",EDGE,"E174.MirrorCS"),sQuery(id+"F4.wireOp",EDGE,"E175.MirrorCS"),sQuery(id+"F4.wireOp",EDGE,"E176.MirrorCS"),sQuery(id+"F4.wireOp",EDGE,"E63.MirrorCS"),sQuery(id+"F4.wireOp",EDGE,"E143.MirrorCS"),sQuery(id+"F4.wireOp",EDGE,"E64.MirrorCS"),sQuery(id+"F4.wireOp",EDGE,"E177.MirrorCS"),sQuery(id+"F4.wireOp",EDGE,"E178.MirrorCS")])]});
            transform(context, id + "F8", {"entities" : qUnion([Q0]), "transformType" : TransformType.TRANSLATION_3D, "dx" : -120 * mm, "dy" : 0 * mm, "dz" : 0 * mm, "makeCopy" : false});
        }
        {
            var Q0;
            {var subQ5=sQuery(id+"F4.wireOp",EDGE,"E45.filletArc");Q0=makeQuery(id+"F4.imprint","IMPRINT",FACE,{"disambiguationData":[TD([[makeQuery(id+"F4.imprint","IMPRINT",EDGE,{"derivedFrom":subQ5}),1.0]])]});}
            var Q1;
            Q1=makeQuery(id+"F4.imprint","IMPRINT",FACE,{"disambiguationData":[TD([[makeQuery(id+"F4.imprint","IMPRINT",EDGE,{"derivedFrom":sQuery(id+"F4.wireOp",EDGE,"E92.MirrorC")}),1.0]])]});
            var Q2;
            Q2=makeQuery(id+"F4.imprint","IMPRINT",FACE,{"disambiguationData":[TD([[makeQuery(id+"F4.imprint","IMPRINT",EDGE,{"derivedFrom":sQuery(id+"F4.wireOp",EDGE,"E50")}),-1.0]])]});
            var Q3;
            Q3=makeQuery(id+"F4.imprint","IMPRINT",FACE,{"disambiguationData":[TD([[makeQuery(id+"F4.imprint","IMPRINT",EDGE,{"derivedFrom":sQuery(id+"F4.wireOp",EDGE,"E49")}),-1.0]])]});
            var Q4;
            Q4=makeQuery(id+"F4.imprint","IMPRINT",FACE,{"disambiguationData":[TD([[makeQuery(id+"F4.imprint","IMPRINT",EDGE,{"derivedFrom":sQuery(id+"F4.wireOp",EDGE,"E124.MirrorCS")}),-1.0]])]});
            var Q5;
            Q5=makeQuery(id+"F4.imprint","IMPRINT",FACE,{"disambiguationData":[TD([[makeQuery(id+"F4.imprint","IMPRINT",EDGE,{"derivedFrom":sQuery(id+"F4.wireOp",EDGE,"E129.MirrorCS")}),-1.0]])]});
            var Q6;
            Q6=makeQuery(id+"F4.imprint","IMPRINT",FACE,{"disambiguationData":[TD([[makeQuery(id+"F4.imprint","IMPRINT",EDGE,{"derivedFrom":sQuery(id+"F4.wireOp",EDGE,"E147.MirrorC")}),-1.0]])]});
            var Q7;
            Q7=makeQuery(id+"F4.imprint","IMPRINT",FACE,{"disambiguationData":[TD([[makeQuery(id+"F4.imprint","IMPRINT",EDGE,{"derivedFrom":sQuery(id+"F4.wireOp",EDGE,"E130.MirrorCS")}),1.0]])]});
            var Q8;
            Q8=makeQuery(id+"F4.imprint","IMPRINT",FACE,{"disambiguationData":[TD([[makeQuery(id+"F4.imprint","IMPRINT",EDGE,{"derivedFrom":sQuery(id+"F4.wireOp",EDGE,"E123.MirrorCS")}),-1.0]])]});
            var Q9;
            Q9=makeQuery(id+"F4.imprint","IMPRINT",FACE,{"disambiguationData":[TD([[makeQuery(id+"F4.imprint","IMPRINT",EDGE,{"derivedFrom":sQuery(id+"F4.wireOp",EDGE,"E60.MirrorCS")}),1.0]])]});
            var Q10;
            {var subQ5=sQuery(id+"F4.wireOp",EDGE,"E48.filletArc");Q10=makeQuery(id+"F4.imprint","IMPRINT",FACE,{"disambiguationData":[TD([[makeQuery(id+"F4.imprint","IMPRINT",EDGE,{"derivedFrom":subQ5}),1.0]])]});}
            extrude(context, id + "F9", {"entities" : qUnion([Q0, Q1, Q2, Q3, Q4, Q5, Q6, Q7, Q8, Q9, Q10]), "depth" : 200 * mm});
        }
    });
